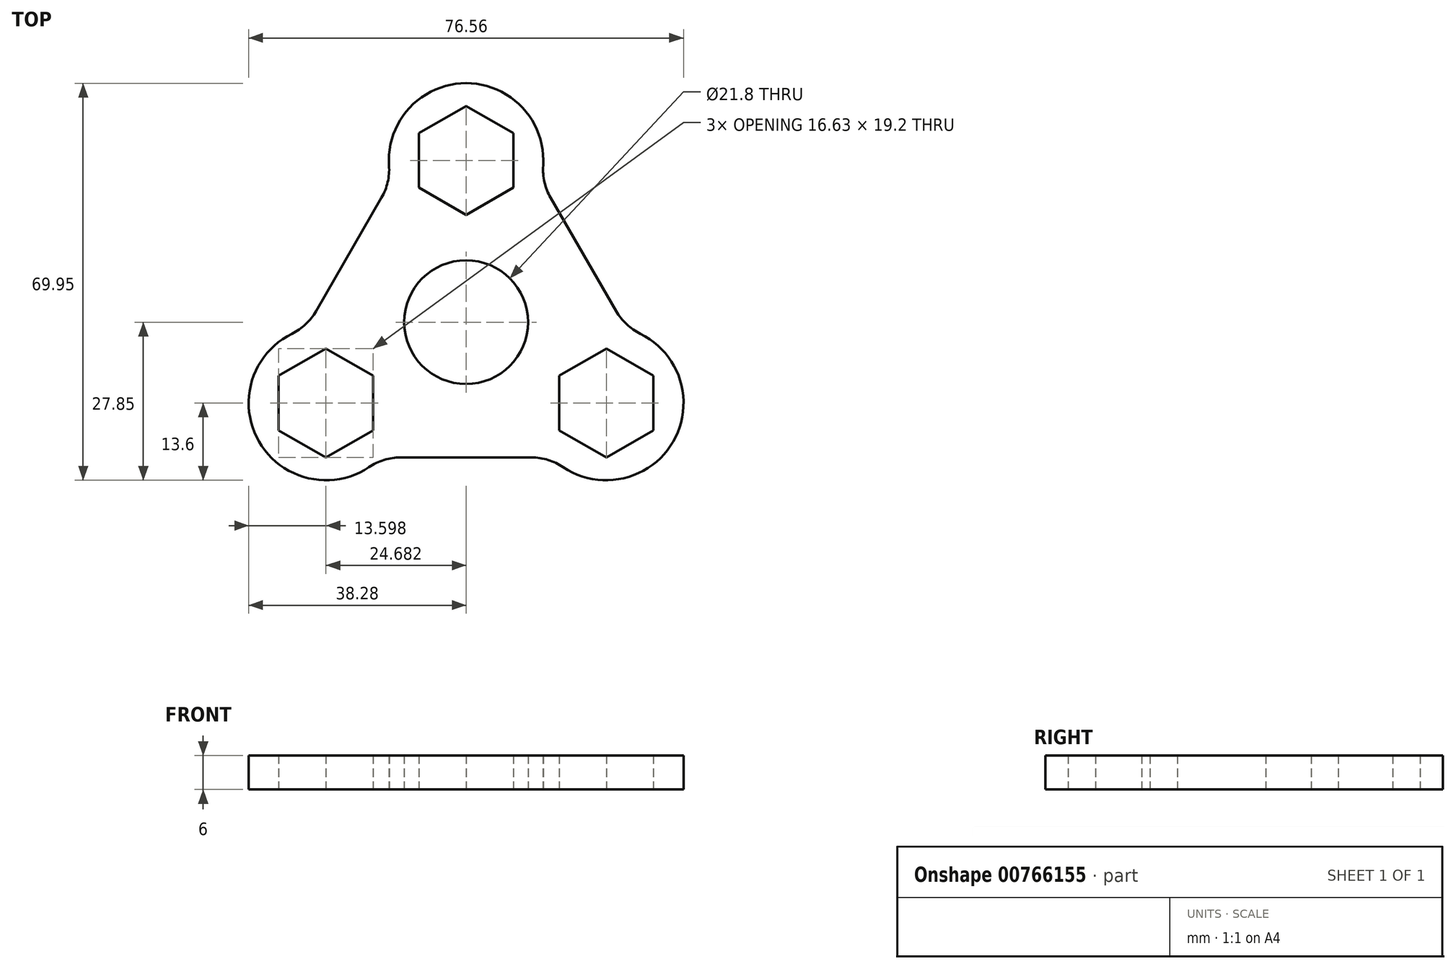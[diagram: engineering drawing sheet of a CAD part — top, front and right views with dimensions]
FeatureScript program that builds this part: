
annotation { "Feature Type Name" : "Feature", "Feature Type Description" : "" }
export const myFeature = defineFeature(function(context is Context, id is Id, definition is map)
    precondition{}
    {
        {
            assignVariable(context, id + "F0", {"name" : "bearingH", "anyValue" : 6});
        }
        {
            var Q0;
            Q0=qCreatedBy(makeId("Top.planeOp"),FACE);
            var sketch = newSketch(context, id + "F1", { "sketchPlane" : qUnion([Q0])});
            skCircle(sketch, "E0", {"center": v(0, 0) * mm, "radius": 10.9 * mm});
            skLineSegment(sketch, "E1", {"start": v(0, 0) * mm, "end": v(0, 28.5) * mm, "construction": true});
            skLineSegment(sketch, "E2", {"start": v(0, 0) * mm, "end": v(24.68, -14.25) * mm, "construction": true});
            skLineSegment(sketch, "E3", {"start": v(0, 0) * mm, "end": v(-24.68, -14.25) * mm, "construction": true});
            skCircle(sketch, "E4.cCircle", {"center": v(0, 28.5) * mm, "radius": 8.31 * mm, "construction": true});
            skLineSegment(sketch, "E4.0", {"start": v(8.31, 33.3) * mm, "end": v(8.31, 23.7) * mm});
            skLineSegment(sketch, "E4.1", {"start": v(8.31, 23.7) * mm, "end": v(0, 18.9) * mm});
            skLineSegment(sketch, "E4.2", {"start": v(0, 18.9) * mm, "end": v(-8.31, 23.7) * mm});
            skLineSegment(sketch, "E4.3", {"start": v(-8.31, 23.7) * mm, "end": v(-8.31, 33.3) * mm});
            skLineSegment(sketch, "E4.4", {"start": v(-8.31, 33.3) * mm, "end": v(0, 38.1) * mm});
            skLineSegment(sketch, "E4.5", {"start": v(0, 38.1) * mm, "end": v(8.31, 33.3) * mm});
            skPoint(sketch, "E4.0.midPoint", {"position": v(8.31, 28.5) * mm});
            skCircle(sketch, "E5.cCircle", {"center": v(24.68, -14.25) * mm, "radius": 8.31 * mm, "construction": true});
            skLineSegment(sketch, "E5.0", {"start": v(24.68, -4.65) * mm, "end": v(33, -9.45) * mm});
            skLineSegment(sketch, "E5.1", {"start": v(33, -9.45) * mm, "end": v(33, -19.05) * mm});
            skLineSegment(sketch, "E5.2", {"start": v(33, -19.05) * mm, "end": v(24.68, -23.85) * mm});
            skLineSegment(sketch, "E5.3", {"start": v(24.68, -23.85) * mm, "end": v(16.37, -19.05) * mm});
            skLineSegment(sketch, "E5.4", {"start": v(16.37, -19.05) * mm, "end": v(16.37, -9.45) * mm});
            skLineSegment(sketch, "E5.5", {"start": v(16.37, -9.45) * mm, "end": v(24.68, -4.65) * mm});
            skPoint(sketch, "E5.0.midPoint", {"position": v(28.84, -7.05) * mm});
            skCircle(sketch, "E6.cCircle", {"center": v(-24.68, -14.25) * mm, "radius": 8.31 * mm, "construction": true});
            skLineSegment(sketch, "E6.0", {"start": v(-24.68, -4.65) * mm, "end": v(-16.37, -9.45) * mm});
            skLineSegment(sketch, "E6.1", {"start": v(-16.37, -9.45) * mm, "end": v(-16.37, -19.05) * mm});
            skLineSegment(sketch, "E6.2", {"start": v(-16.37, -19.05) * mm, "end": v(-24.68, -23.85) * mm});
            skLineSegment(sketch, "E6.3", {"start": v(-24.68, -23.85) * mm, "end": v(-33, -19.05) * mm});
            skLineSegment(sketch, "E6.4", {"start": v(-33, -19.05) * mm, "end": v(-33, -9.45) * mm});
            skLineSegment(sketch, "E6.5", {"start": v(-33, -9.45) * mm, "end": v(-24.68, -4.65) * mm});
            skPoint(sketch, "E6.0.midPoint", {"position": v(-20.52, -7.05) * mm});
            skArc(sketch, "E7", {"start": v(13.57, 27.59) * mm, "mid": v(0, 42.1) * mm, "end": v(-13.57, 27.59) * mm});
            skArc(sketch, "E8", {"start": v(17.1, -25.54) * mm, "mid": v(36.46, -21.05) * mm, "end": v(30.68, -2.04) * mm});
            skArc(sketch, "E9", {"start": v(-30.68, -2.04) * mm, "mid": v(-36.46, -21.05) * mm, "end": v(-17.1, -25.54) * mm});
            skLineSegment(sketch, "E10", {"start": v(-26.42, 1.93) * mm, "end": v(-14.89, 21.92) * mm});
            skLineSegment(sketch, "E11", {"start": v(14.89, 21.92) * mm, "end": v(26.42, 1.93) * mm});
            skLineSegment(sketch, "E12", {"start": v(11.54, -23.85) * mm, "end": v(-11.54, -23.85) * mm});
            skPoint(sketch, "E13.visualSharp", {"position": v(-13.13, 24.96) * mm});
            skArc(sketch, "E13.filletArc", {"start": v(-14.89, 21.92) * mm, "mid": v(-13.8, 24.65) * mm, "end": v(-13.57, 27.59) * mm});
            skPoint(sketch, "E14.visualSharp", {"position": v(-28.18, -1.1) * mm});
            skArc(sketch, "E14.filletArc", {"start": v(-30.68, -2.04) * mm, "mid": v(-28.25, -0.37) * mm, "end": v(-26.42, 1.93) * mm});
            skPoint(sketch, "E15.visualSharp", {"position": v(-15.05, -23.85) * mm});
            skArc(sketch, "E15.filletArc", {"start": v(-11.54, -23.85) * mm, "mid": v(-14.45, -24.28) * mm, "end": v(-17.1, -25.54) * mm});
            skPoint(sketch, "E16.visualSharp", {"position": v(15.05, -23.85) * mm});
            skArc(sketch, "E16.filletArc", {"start": v(17.1, -25.54) * mm, "mid": v(14.45, -24.28) * mm, "end": v(11.54, -23.85) * mm});
            skPoint(sketch, "E17.visualSharp", {"position": v(13.13, 24.96) * mm});
            skArc(sketch, "E17.filletArc", {"start": v(13.57, 27.59) * mm, "mid": v(13.8, 24.65) * mm, "end": v(14.89, 21.92) * mm});
            skPoint(sketch, "E18.visualSharp", {"position": v(28.18, -1.1) * mm});
            skArc(sketch, "E18.filletArc", {"start": v(26.42, 1.93) * mm, "mid": v(28.25, -0.37) * mm, "end": v(30.68, -2.04) * mm});
            skSolve(sketch);
        }
        {
            var Q0;
            Q0=makeQuery(id+"F1.imprint","IMPRINT",FACE,{"disambiguationData":[TD([[makeQuery(id+"F1.imprint","IMPRINT",EDGE,{"derivedFrom":sQuery(id+"F1.wireOp",EDGE,"E0")}),-1.0]])]});
            extrude(context, id + "F2", {"entities" : qUnion([Q0]), "depth" : (getVariable(context, 'bearingH')) * mm, "offsetDistance" : 25 * mm});
        }
    });
